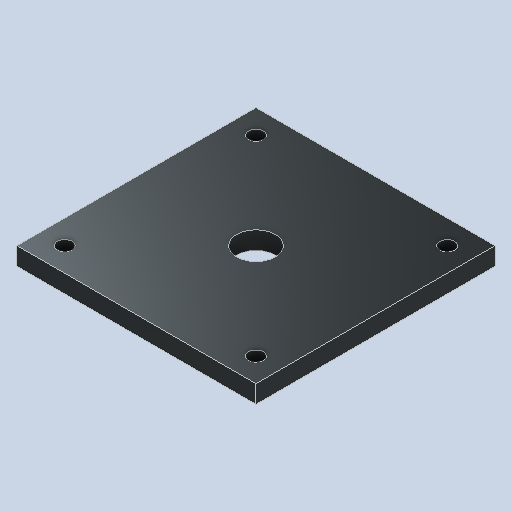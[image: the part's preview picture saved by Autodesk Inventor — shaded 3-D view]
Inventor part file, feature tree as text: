
AUTODESK INVENTOR PART (.ipt)
format: ipt  version: 2023 (Build 270158000, 158)  size: 134,656 bytes
history: native  units: mm
features: sketch x3, hole x2, other x1, extrude x1
ambient origin geometry x8: Origin, YZ Plane, XZ Plane, XY Plane, X Axis, Y Axis, Z Axis, Center Point
bodies: Body1 (feature_tree)
feature tree (7):
  other  "Sólido1"
  extrude  "Extrusão1"  Depth=80.0mm
  hole  "Furo1"  [1 undecoded]
  hole  "Furo2"  [1 undecoded]
  sketch  "Esboço1"  dims[d0=80.0mm d1=80.0mm]
  sketch  "Esboço2"  dims[d2=6.0mm d3=0.0mm d4=8.0mm]
  sketch  "Esboço3"  dims[d5=8.0mm d6=8.0mm d7=8.0mm d8=8.0mm d9=8.0mm d10=8.0mm d11=8.0mm d12=5.0mm d13=6.0mm d14=4.0mm d15=2.0mm d16=90.0deg d17=0.5mm d18=20.594885mm d19=80.0mm d20=40.0mm d21=40.0mm d22=13.0mm d23=6.0mm d24=4.0mm d25=2.0mm d26=90.0deg d27=8.0mm d28=20.594885mm]
note: 2 required parameter values undecoded (feature->parameter linkage not recoverable at this tier; creation-order binding heuristic only, values carry confidence <= 0.55)
